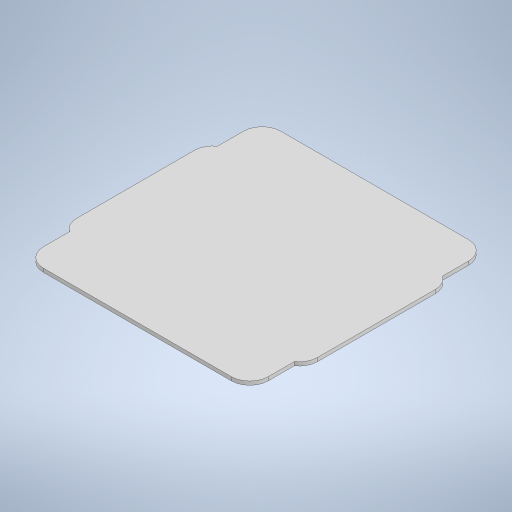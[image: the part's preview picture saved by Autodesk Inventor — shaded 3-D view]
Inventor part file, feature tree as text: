
AUTODESK INVENTOR PART (.ipt)
format: ipt  version: 2024.2 (Build 282272000, 272)  size: 285,184 bytes
history: native  units: in
note: dims shown in document units (in); Inventor stores cm internally (conversion verified against a paired STEP export)
features: extrude x2, sketch x2, projected_geometry x1
ambient origin geometry x8: Origin, YZ Plane, XZ Plane, XY Plane, X Axis, Y Axis, Z Axis, Center Point
bodies: Solid1 (feature_tree)
feature tree (5):
  extrude  "Extrusion1"  Depth=7.063in
  extrude  "Extrusion2"  Depth=0.125in
  sketch  "Sketch1"  dims[d0=6.643in d1=7.063in]
  sketch  "Sketch2"  dims[d2=0.272in d4=0.125in d5=0.125in d6=0.125in d7=0.125in d8=0.0in d9=0.5in d10=0.5in d11=0.5in d12=0.5in d13=0.5in d14=0.5in d15=0.5in d16=0.5in d17=0.125in d18=0.0in]
  projected_geometry  "Projected Loop1"
